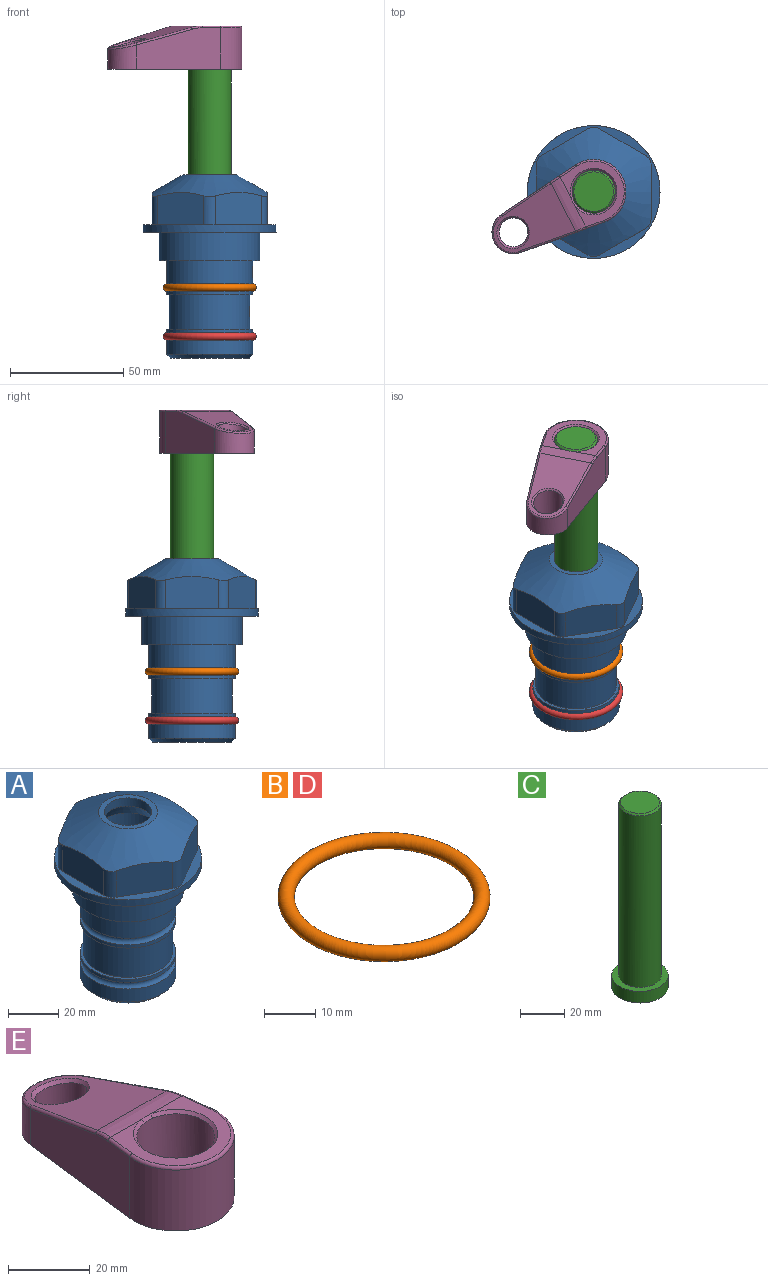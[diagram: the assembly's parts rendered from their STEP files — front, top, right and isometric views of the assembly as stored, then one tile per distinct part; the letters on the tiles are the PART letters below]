
ASSEMBLY  parts=5 mates=4
PART A: 36 faces, bbox 58.7x58.7x81 mm
  f0: cylinder r=17.78mm len=35.56mm, axis (0,0,1), area 1670.8mm2, adj f23,f24,f31
  f1: cylinder r=19.05mm len=38.1mm, axis (0,0,1), area 1191.9mm2, adj f26,f27,f30
  f2: plane 58.66x58.66mm, normal (0,0,-1), area 1150.6mm2, adj f3,f28
  f3: cylinder r=29.33mm len=58.66mm, axis (0,0,-1), area 585.1mm2, adj f2,f4
  f4: plane 58.66x58.66mm, normal (0,0,1), area 475.9mm2, adj f3,f5,f6,f7,f8,f9,f10,f11
  f5: plane 20.32x14.34mm, normal (-0.5,0.87,0), area 324.4mm2, adj f4,f15,f16,f17
  f6: plane 20.32x14.34mm, normal (0.5,0.87,0), area 324.4mm2, adj f4,f14,f15,f17
  f7: plane 23.48x14.34mm, normal (1,0,0), area 324.4mm2, adj f4,f13,f14,f17
  f8: plane 20.32x14.34mm, normal (0.5,-0.87,0), area 324.4mm2, adj f4,f12,f13,f17
  f9: plane 20.32x14.34mm, normal (-0.5,-0.87,0), area 324.4mm2, adj f4,f11,f12,f17
  f10: plane 23.48x14.34mm, normal (-1,0,0), area 324.4mm2, adj f4,f11,f16,f17
  f11: cylinder r=5.08mm len=12.85mm, axis (0,0,-1), area 67.2mm2, adj f4,f9,f10,f17
  f12: cylinder r=5.08mm len=12.85mm, axis (0,0,-1), area 67.2mm2, adj f4,f8,f9,f17
  f13: cylinder r=5.08mm len=12.85mm, axis (0,0,-1), area 67.2mm2, adj f4,f7,f8,f17
  f14: cylinder r=5.08mm len=12.85mm, axis (0,0,-1), area 67.2mm2, adj f4,f6,f7,f17
  f15: cylinder r=5.08mm len=12.85mm, axis (0,0,-1), area 67.2mm2, adj f4,f5,f6,f17
  f16: cylinder r=5.08mm len=12.85mm, axis (0,0,-1), area 67.2mm2, adj f4,f5,f10,f17
  f17: cone r=11.73mm half-angle=60deg, axis (0,0,-1), area 2071.8mm2, adj f5,f6,f7,f8,f9,f10,f11,f12
  f18: plane 23.46x23.46mm, normal (0,0,1), area 147.4mm2, adj f17,f35
  f19: plane 34.93x34.93mm, normal (0,0,-1), area 958mm2, adj f29
  f20: cylinder r=19.05mm len=38.1mm, axis (0,0,1), area 760.1mm2, adj f21,f29
  f21: torus R=19.05mm, axis (0,0,1), area 565.3mm2, adj f20,f22
  f22: cylinder r=19.05mm len=38.1mm, axis (0,0,1), area 190mm2, adj f21,f23
  f23: plane 38.1x38.1mm, normal (0,0,1), area 146.9mm2, adj f0,f22
  f24: plane 38.1x38.1mm, normal (0,0,-1), area 146.9mm2, adj f0,f25
  f25: cylinder r=19.05mm len=38.1mm, axis (0,0,1), area 190mm2, adj f24,f26
  f26: torus R=19.05mm, axis (0,0,1), area 565.3mm2, adj f1,f25
  f27: plane 44.45x44.45mm, normal (0,0,-1), area 411.7mm2, adj f1,f28
  f28: cylinder r=22.23mm len=44.45mm, axis (0,0,1), area 1773.5mm2, adj f2,f27
  f29: cone r=19.05mm half-angle=45deg, axis (0,0,1), area 257.5mm2, adj f19,f20
  f30: cylinder r=3.17mm len=6.75mm, axis (-1,0,0), area 128mm2, adj f1,f33
  f31: cylinder r=3.17mm len=6.35mm, axis (-1,0,0), area 102.5mm2, adj f0,f33
  f32: plane 25.4x25.4mm, normal (0,0,1), area 506.7mm2, adj f33
  f33: cylinder r=12.7mm len=66.42mm, axis (0,0,-1), area 5236.2mm2, adj f30,f31,f32,f34
  f34: cone r=9.53mm half-angle=30deg, axis (0,0,-1), area 443.4mm2, adj f33,f35
  f35: cylinder r=9.53mm len=19.05mm, axis (0,0,-1), area 240.9mm2, adj f18,f34
PART B: 1 faces, bbox 44.7x44.7x3.2 mm
  f0: torus R=19.05mm, axis (0,0,1), area 1193.9mm2
PART C: 6 faces, bbox 25.4x25.4x101.6 mm
  f0: plane 17.46x17.46mm, normal (0,0,1), area 239.5mm2, adj f5
  f1: plane 25.4x25.4mm, normal (0,0,-1), area 506.7mm2, adj f2
  f2: cylinder r=12.7mm len=25.4mm, axis (0,0,1), area 506.7mm2, adj f1,f3
  f3: plane 25.4x25.4mm, normal (0,0,1), area 221.7mm2, adj f2,f4
  f4: cylinder r=9.53mm len=94.46mm, axis (0,0,1), area 5653mm2, adj f3,f5
  f5: cone r=8.73mm half-angle=45deg, axis (0,0,-1), area 64.4mm2, adj f0,f4
PART D: same geometry as B
PART E: 31 faces, bbox 31.7x65.5x19.8 mm
  f0: plane 39.12x18.26mm, normal (0.99,0.12,0), area 612.2mm2, adj f1,f4,f7,f11,f13,f15
  f1: cylinder r=9.53mm len=18.91mm, axis (0,0,-1), area 296.1mm2, adj f0,f2,f7,f17
  f2: plane 39.12x18.26mm, normal (-0.99,0.12,0), area 612.2mm2, adj f1,f4,f7,f12,f14,f16
  f3: cylinder r=6.35mm len=12.7mm, axis (0,0,-1), area 362.4mm2, adj f7,f18
  f4: cylinder r=14.29mm len=28.58mm, axis (0,0,-1), area 882.2mm2, adj f0,f2,f7,f10
  f5: cylinder r=9.53mm len=19.05mm, axis (0,0,-1), area 1092.6mm2, adj f7,f19,f20
  f6: plane 26.99x23.69mm, normal (0,0,1), area 216.2mm2, adj f9,f10,f11,f12,f19
  f7: plane 63.5x28.58mm, normal (0,0,-1), area 661.8mm2, adj f0,f1,f2,f3,f4,f5,f22,f23
  f8: plane 33.52x23.6mm, normal (0,0.26,0.97), area 486mm2, adj f9,f15,f16,f17,f18
  f9: cylinder r=19.05mm len=24.72mm, axis (1,0,0), area 120.4mm2, adj f6,f8,f13,f14,f20
  f10: torus R=13.49mm, axis (0,0,1), area 59mm2, adj f4,f6,f11,f12
  f11: cylinder r=0.79mm len=8.67mm, axis (0.12,-0.99,0), area 10.8mm2, adj f0,f6,f10,f13
  f12: cylinder r=0.79mm len=8.67mm, axis (0.12,0.99,0), area 10.8mm2, adj f2,f6,f10,f14
  f13: bspline ~4.95x1.42mm, area 6.1mm2, adj f0,f9,f11,f15
  f14: bspline ~4.95x1.42mm, area 6.1mm2, adj f2,f9,f12,f16
  f15: cylinder r=0.79mm len=25.95mm, axis (0.12,-0.96,0.26), area 32.9mm2, adj f0,f8,f13,f17
  f16: cylinder r=0.79mm len=25.95mm, axis (0.12,0.96,-0.26), area 32.9mm2, adj f2,f8,f14,f17
  f17: bspline ~18.91x8.38mm, area 30mm2, adj f1,f8,f15,f16
  f18: bspline ~14.29x14.29mm, area 48.3mm2, adj f3,f8
  f19: cone r=9.53mm half-angle=45deg, axis (0,0,1), area 66.5mm2, adj f5,f6,f20
  f20: bspline ~3.22x0.96mm, area 3.5mm2, adj f5,f9,f19
  f21: plane 2.75x2.72mm, normal (0,0,-1), area 2.9mm2, adj f23,f25,f28
  f22: plane 23.05x15.88mm, normal (-0.99,-0.12,0), area 323.6mm2, adj f7,f25,f26,f27,f28,f29
  f23: plane 23.05x15.88mm, normal (0.99,-0.12,0), area 323.6mm2, adj f7,f21,f25,f27,f28,f30
  f24: cylinder r=9.53mm len=10.69mm, axis (0,0,-1), area 114.7mm2, adj f7,f27,f29,f30
  f25: cylinder r=12.7mm len=20.59mm, axis (0,0,-1), area 381.1mm2, adj f7,f21,f22,f23,f26,f28
  f26: plane 2.75x2.72mm, normal (0,0,-1), area 2.9mm2, adj f22,f25,f28
  f27: plane 19.72x18.37mm, normal (0,-0.26,-0.97), area 291.8mm2, adj f22,f23,f24,f28,f29,f30
  f28: cylinder r=15.88mm len=19.92mm, axis (1,0,0), area 54.8mm2, adj f21,f22,f23,f25,f26,f27
  f29: cylinder r=1.59mm len=11mm, axis (0,0,-1), area 34.7mm2, adj f7,f22,f24,f27
  f30: cylinder r=1.59mm len=11mm, axis (0,0,-1), area 34.7mm2, adj f7,f23,f24,f27
PLACE A at identity fixed
PLACE B at identity
PLACE C rot(axis=(0,0,1),116.9deg) t=(0,0,27.55)mm
PLACE D t=(0,0,-21.59)mm
PLACE E rot(axis=(0,0,1),116.9deg) t=(0,0,27.55)mm
MATE fastened D.f0 <-> A.f0  axis (0,0,1) through (0,0,-46.1)mm
MATE fastened A.f0 <-> B.f0  axis (0,0,1) through (0,0,-24.51)mm
MATE cylindrical A.f0 <-> C.f2  axis (0,0,1) through (0,0,-50.55)mm
MATE fastened C.f2 <-> E.f4  axis (0,0,1) through (0,0,91.05)mm
